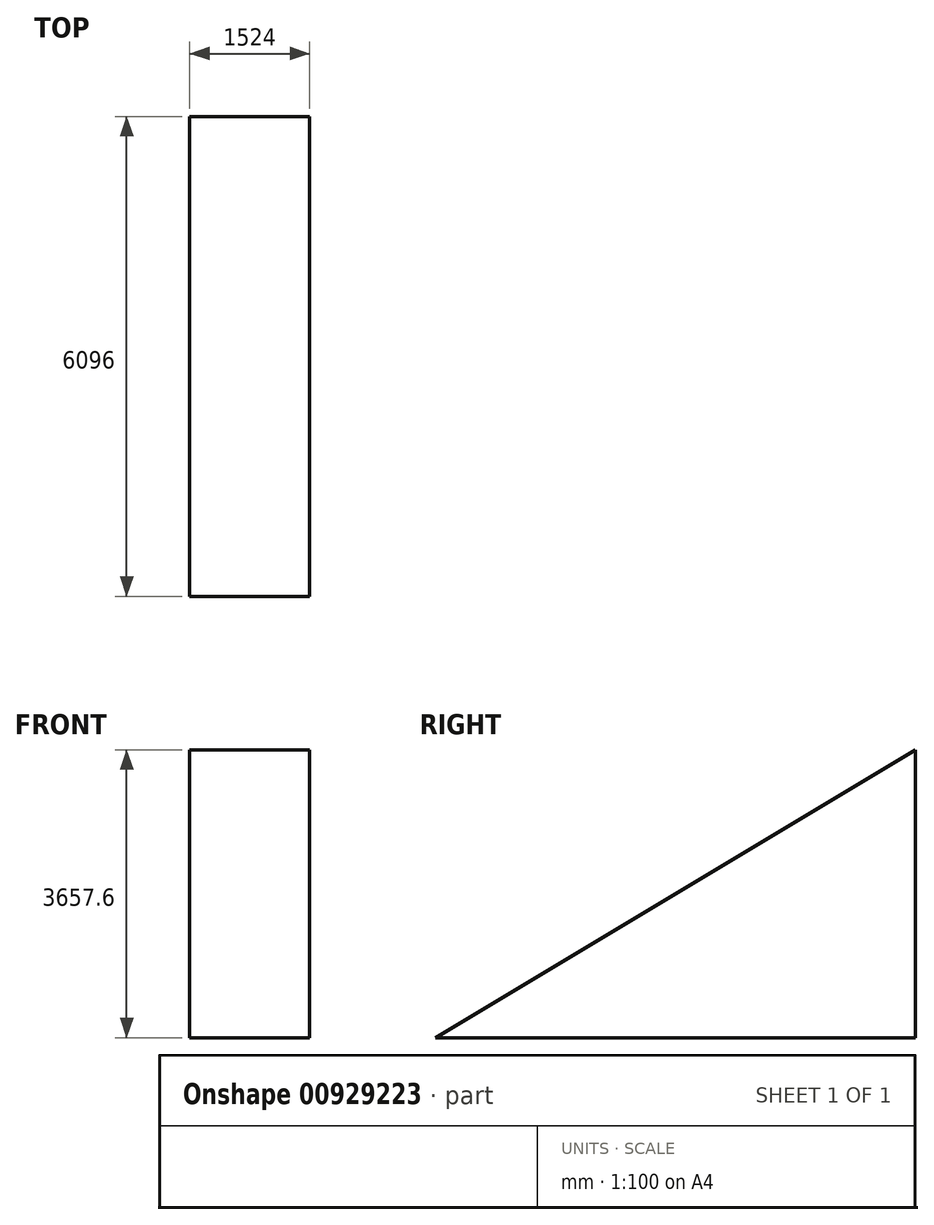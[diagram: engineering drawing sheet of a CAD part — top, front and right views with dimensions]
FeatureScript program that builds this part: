
annotation { "Feature Type Name" : "Feature", "Feature Type Description" : "" }
export const myFeature = defineFeature(function(context is Context, id is Id, definition is map)
    precondition{}
    {
        {
            var Q0;
            Q0=qCreatedBy(makeId("Right.planeOp"),FACE);
            var sketch = newSketch(context, id + "F0", { "sketchPlane" : qUnion([Q0])});
            skLineSegment(sketch, "E0", {"start": v(0, 0) * mm, "end": v(2996.23, 0) * mm});
            skLineSegment(sketch, "E1", {"start": v(2996.23, 0) * mm, "end": v(2996.23, 3657.6) * mm});
            skLineSegment(sketch, "E2", {"start": v(2996.23, 3657.6) * mm, "end": v(-3099.77, 0) * mm});
            skLineSegment(sketch, "E3", {"start": v(-3099.77, 0) * mm, "end": v(0, 0) * mm});
            skSolve(sketch);
        }
        {
            var Q0;
            Q0 = qSketchRegion(id + "F0", true);
            extrude(context, id + "F1", {"entities" : qUnion([Q0]), "endBound" : BoundingType.SYMMETRIC, "depth" : 1524 * mm, "offsetDistance" : 25.4 * mm});
        }
    });
